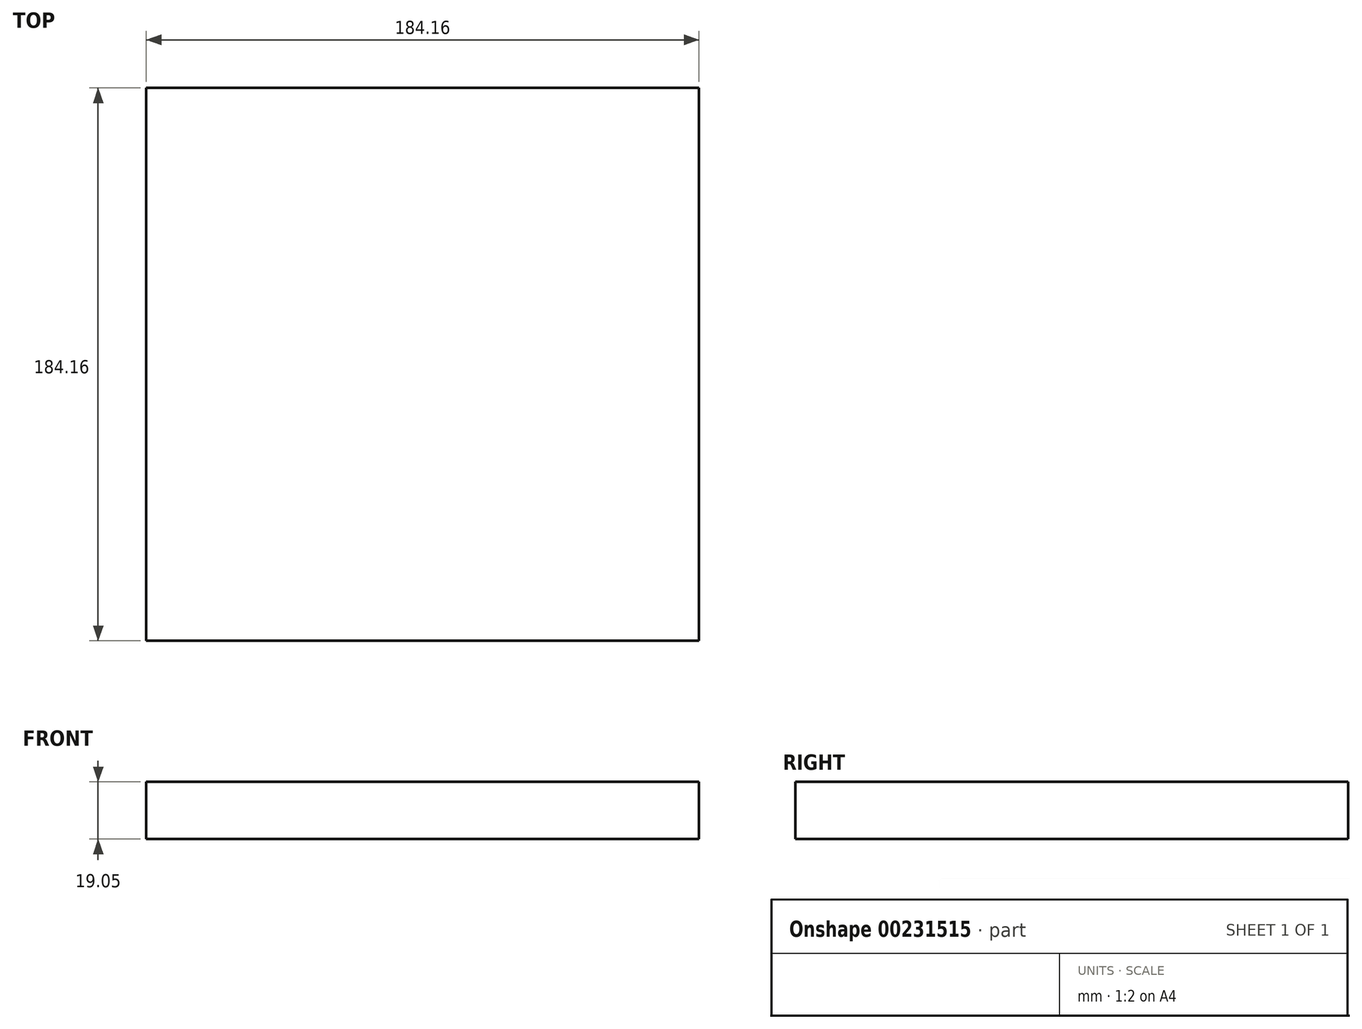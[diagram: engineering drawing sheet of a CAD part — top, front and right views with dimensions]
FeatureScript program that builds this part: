
annotation { "Feature Type Name" : "Feature", "Feature Type Description" : "" }
export const myFeature = defineFeature(function(context is Context, id is Id, definition is map)
    precondition{}
    {
        {
            var Q0;
            Q0=qCreatedBy(makeId("Top.planeOp"),FACE);
            var sketch = newSketch(context, id + "F0", { "sketchPlane" : qUnion([Q0])});
            skLineSegment(sketch, "E0.bottom", {"start": v(92.08, 92.08) * mm, "end": v(-92.07, 92.08) * mm});
            skLineSegment(sketch, "E0.top", {"start": v(92.08, -92.07) * mm, "end": v(-92.08, -92.07) * mm});
            skLineSegment(sketch, "E0.left", {"start": v(92.08, 92.08) * mm, "end": v(92.08, -92.07) * mm});
            skLineSegment(sketch, "E0.right", {"start": v(-92.07, 92.08) * mm, "end": v(-92.08, -92.07) * mm});
            skPoint(sketch, "E0.middle", {"position": v(0, 0) * mm});
            skSolve(sketch);
        }
        {
            var Q0;
            Q0 = qSketchRegion(id + "F0", true);
            extrude(context, id + "F1", {"entities" : qUnion([Q0]), "depth" : 19.05 * mm});
        }
    });
